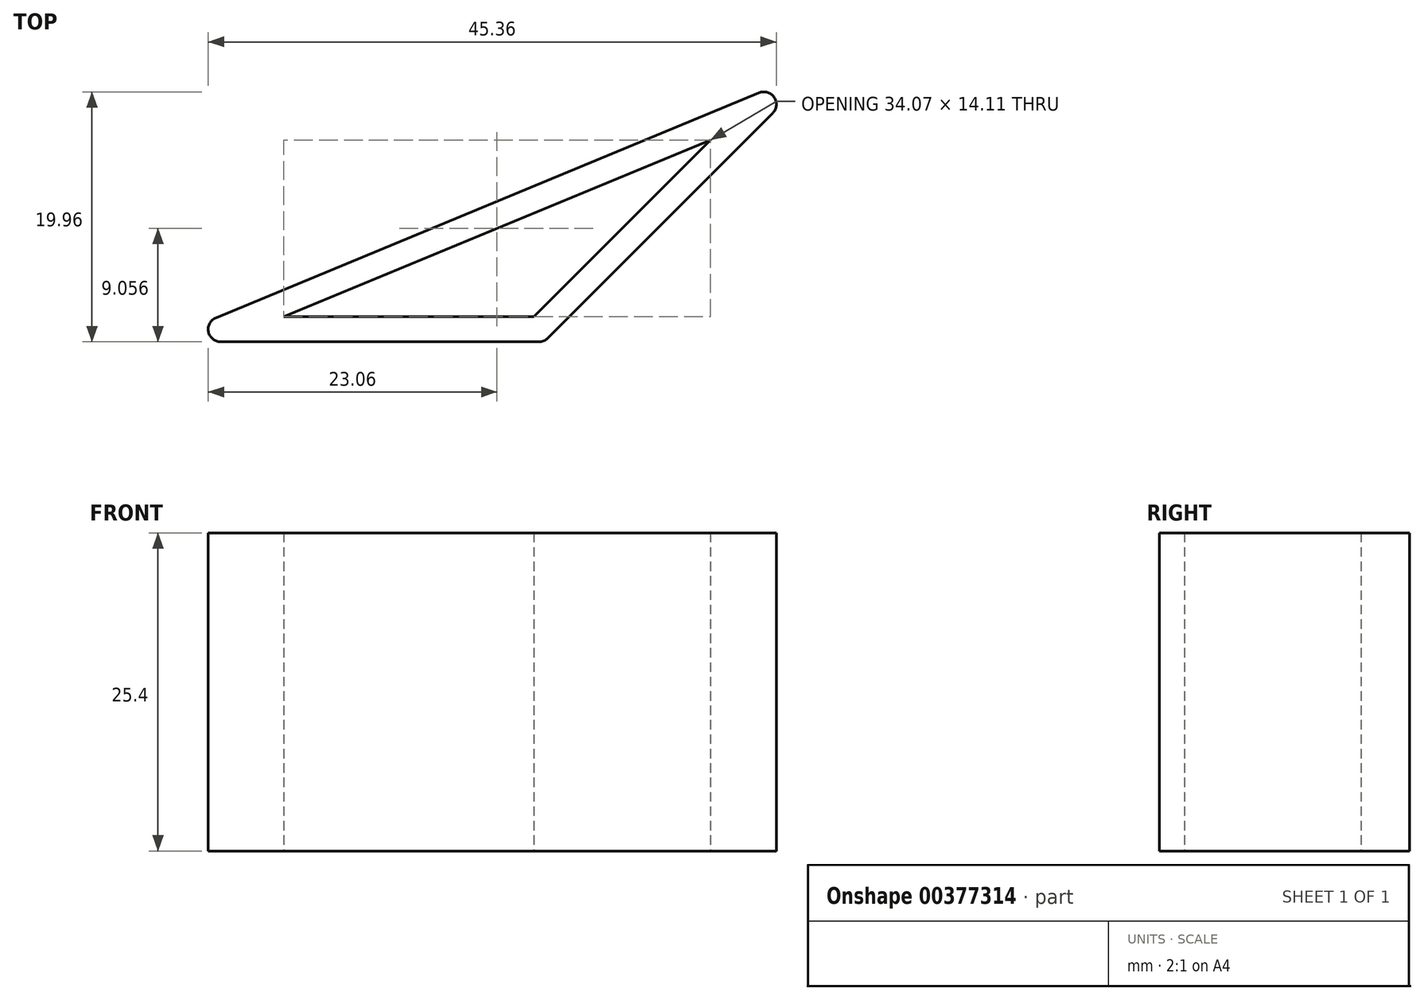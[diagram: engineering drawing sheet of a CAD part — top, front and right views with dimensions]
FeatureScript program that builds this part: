
annotation { "Feature Type Name" : "Feature", "Feature Type Description" : "" }
export const myFeature = defineFeature(function(context is Context, id is Id, definition is map)
    precondition{}
    {
        {
            var Q0;
            Q0=qCreatedBy(makeId("Top.planeOp"),FACE);
            var sketch = newSketch(context, id + "F0", { "sketchPlane" : qUnion([Q0])});
            skLineSegment(sketch, "E0", {"start": v(5.03, 0) * mm, "end": v(30.43, 0) * mm});
            skLineSegment(sketch, "E1", {"start": v(31.13, 0.3) * mm, "end": v(49.1, 18.25) * mm});
            skLineSegment(sketch, "E2", {"start": v(48, 19.88) * mm, "end": v(4.64, 1.92) * mm});
            skPoint(sketch, "E3.visualSharp", {"position": v(30.84, 0) * mm});
            skArc(sketch, "E3.filletArc", {"start": v(30.43, 0) * mm, "mid": v(30.81, 0.08) * mm, "end": v(31.13, 0.3) * mm});
            skPoint(sketch, "E4.visualSharp", {"position": v(52.65, 21.8) * mm});
            skArc(sketch, "E4.filletArc", {"start": v(49.1, 18.25) * mm, "mid": v(49.22, 19.52) * mm, "end": v(48, 19.88) * mm});
            skPoint(sketch, "E5.visualSharp", {"position": v(0, 0) * mm});
            skArc(sketch, "E5.filletArc", {"start": v(4.64, 1.92) * mm, "mid": v(4.05, 0.8) * mm, "end": v(5.03, 0) * mm});
            skLineSegment(sketch, "E6.0", {"start": v(44.13, 16.11) * mm, "end": v(10.05, 2) * mm});
            skLineSegment(sketch, "E6.1", {"start": v(30.01, 2) * mm, "end": v(44.13, 16.11) * mm});
            skLineSegment(sketch, "E6.2", {"start": v(10.05, 2) * mm, "end": v(30.01, 2) * mm});
            skSolve(sketch);
        }
        {
            var Q0;
            Q0 = qSketchRegion(id + "F0", true);
            extrude(context, id + "F1", {"entities" : qUnion([Q0]), "depth" : 25.4 * mm});
        }
    });
